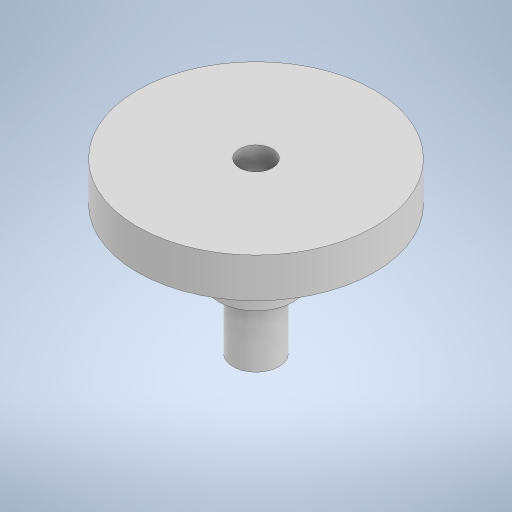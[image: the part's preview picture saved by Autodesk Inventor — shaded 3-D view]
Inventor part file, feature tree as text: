
AUTODESK INVENTOR PART (.ipt)
format: ipt  version: 2023 (Build 270158000, 158)  size: 225,792 bytes
history: native  units: mm
features: revolve x1, sketch x1
ambient origin geometry x8: Origin, YZ Plane, XZ Plane, XY Plane, X Axis, Y Axis, Z Axis, Center Point
bodies: Solid1 (feature_tree)
feature tree (2):
  revolve  "Revolution1"  [1 undecoded]
  sketch  "Sketch1"  dims[d0=2.1mm d1=4.7mm d3=8.0mm d4=2.9mm d5=5.0mm d6=16.4mm d7=15.0mm d8=90.0deg]
note: 1 required parameter value undecoded (feature->parameter linkage not recoverable at this tier; creation-order binding heuristic only, values carry confidence <= 0.55)
